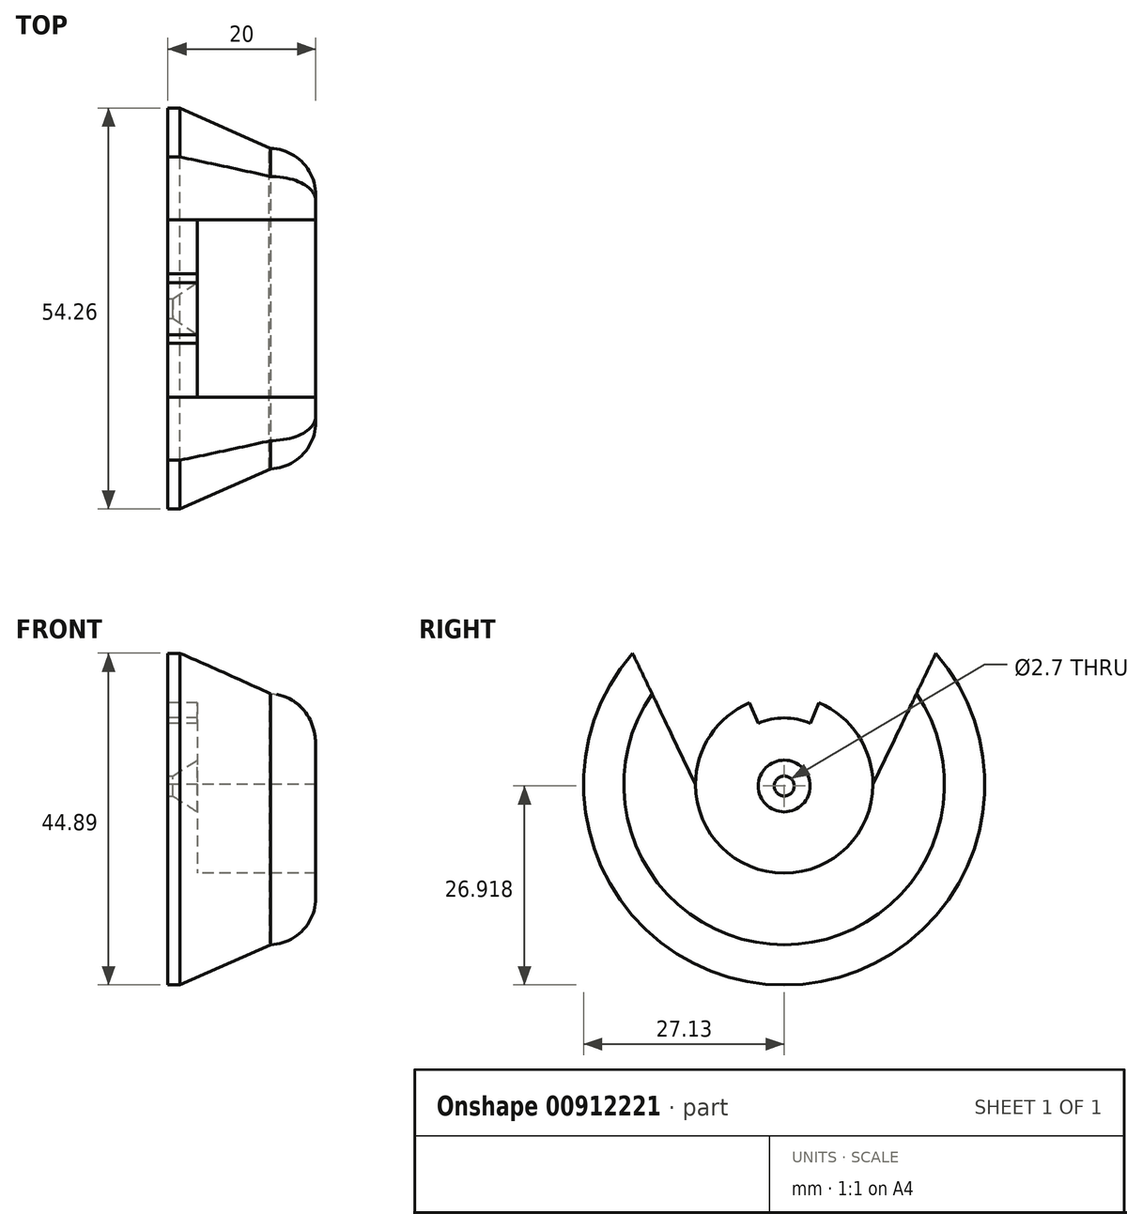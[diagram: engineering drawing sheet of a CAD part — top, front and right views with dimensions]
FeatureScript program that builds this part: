
annotation { "Feature Type Name" : "Feature", "Feature Type Description" : "" }
export const myFeature = defineFeature(function(context is Context, id is Id, definition is map)
    precondition{}
    {
        {
            var Q0;
            Q0=qCreatedBy(makeId("Right.planeOp"),FACE);
            var sketch = newSketch(context, id + "F0", { "sketchPlane" : qUnion([Q0])});
            skCircle(sketch, "E0", {"center": v(0, 0) * mm, "radius": 12 * mm});
            skCircle(sketch, "E1", {"center": v(0, 0) * mm, "radius": 30 * mm});
            skCircle(sketch, "E2", {"center": v(0, 0) * mm, "radius": 15.18 * mm});
            skCircle(sketch, "E3", {"center": v(0, 0) * mm, "radius": 27.13 * mm});
            skCircle(sketch, "E4", {"center": v(0, 0) * mm, "radius": 21.68 * mm});
            skLineSegment(sketch, "E5", {"start": v(12, 0) * mm, "end": v(21.85, 20.55) * mm});
            skLineSegment(sketch, "E6", {"start": v(21.85, 20.55) * mm, "end": v(-21.85, 20.55) * mm});
            skLineSegment(sketch, "E7", {"start": v(-21.85, 20.55) * mm, "end": v(-12, 0) * mm});
            skCircle(sketch, "E8", {"center": v(0, 0) * mm, "radius": 9 * mm});
            skLineSegment(sketch, "E9", {"start": v(0, 0) * mm, "end": v(4.69, 11.05) * mm});
            skLineSegment(sketch, "E10", {"start": v(4.69, 11.05) * mm, "end": v(-4.69, 11.05) * mm});
            skLineSegment(sketch, "E11", {"start": v(-4.69, 11.05) * mm, "end": v(0, 0) * mm});
            skSolve(sketch);
        }
        {
            var Q0;
            Q0=makeQuery(id+"F0.imprint","IMPRINT",FACE,{"disambiguationData":[TD([[makeQuery(id+"F0.imprint","IMPRINT",EDGE,{"derivedFrom":sQuery(id+"F0.wireOp",EDGE,"E0")}),-1.0]])]});
            var Q1;
            {var subQ0=sQuery(id+"F0.wireOp",EDGE,"E5");var subQ1=sQuery(id+"F0.wireOp",EDGE,"E0");var subQ2=makeQuery(id+"F0.imprint","INTERSECT",VERTEX,{"derivedFrom":[subQ1,subQ0]});Q1=makeQuery(id+"F0.imprint","IMPRINT",FACE,{"disambiguationData":[TD([[makeQuery(id+"F0.imprint","IMPRINT",EDGE,{"disambiguationData":[TD([[subQ2,1.0]])],"derivedFrom":subQ1}),-1.0]])]});}
            extrude(context, id + "F1", {"entities" : qUnion([Q0, Q1]), "depth" : 20 * mm, "offsetDistance" : 25 * mm});
        }
        {
            var Q0;
            Q0=makeQuery(id+"F0.imprint","IMPRINT",FACE,{"disambiguationData":[TD([[makeQuery(id+"F0.imprint","IMPRINT",EDGE,{"derivedFrom":sQuery(id+"F0.wireOp",EDGE,"E2")}),-1.0]])]});
            var Q1;
            {var subQ5=sQuery(id+"F0.wireOp",EDGE,"E5");var subQ6=sQuery(id+"F0.wireOp",EDGE,"E2");var subQ7=makeQuery(id+"F0.imprint","INTERSECT",VERTEX,{"derivedFrom":[subQ6,subQ5]});Q1=makeQuery(id+"F0.imprint","IMPRINT",FACE,{"disambiguationData":[TD([[makeQuery(id+"F0.imprint","IMPRINT",EDGE,{"disambiguationData":[TD([[subQ7,-1.0]])],"derivedFrom":subQ6}),-1.0]])]});}
            var Q2;
            {var subQ0=sQuery(id+"F0.wireOp",EDGE,"E6");var subQ1=sQuery(id+"F0.wireOp",EDGE,"E4");var subQ2=makeQuery(id+"F0.imprint","INTERSECT",VERTEX,{"disambiguationData":[OD(0.0)],"derivedFrom":[subQ1,subQ0]});Q2=makeQuery(id+"F0.imprint","IMPRINT",FACE,{"disambiguationData":[TD([[makeQuery(id+"F0.imprint","IMPRINT",EDGE,{"disambiguationData":[TD([[subQ2,-1.0]])],"derivedFrom":subQ1}),1.0]])]});}
            extrude(context, id + "F2", {"entities" : qUnion([Q0, Q1, Q2]), "operationType" : NewBodyOperationType.ADD, "depth" : 20 * mm, "offsetDistance" : 25 * mm});
        }
        {
            var Q0;
            Q0=makeQuery(id+"F2.opExtrude","CAP_EDGE",EDGE,{"disambiguationData":[OSD([sQuery(id+"F0.wireOp",EDGE,"E4")])],"isStart":false});
            fillet(context, id + "F3", {"entities" : qUnion([Q0]), "radius" : 6.3 * mm, "tangentPropagation" : true, "allowEdgeOverflow" : false});
        }
        {
            var Q0;
            Q0=makeQuery(id+"F0.imprint","IMPRINT",FACE,{"disambiguationData":[TD([[makeQuery(id+"F0.imprint","IMPRINT",EDGE,{"derivedFrom":sQuery(id+"F0.wireOp",EDGE,"E3")}),1.0]])]});
            extrude(context, id + "F4", {"entities" : qUnion([Q0]), "operationType" : NewBodyOperationType.ADD, "depth" : 14 * mm, "offsetDistance" : 25 * mm});
        }
        {
            var Q0;
            Q0=makeQuery(id+"F4.opExtrude","CAP_EDGE",EDGE,{"disambiguationData":[OSD([sQuery(id+"F0.wireOp",EDGE,"E3")])],"isStart":false});
            chamfer(context, id + "F5", {"entities" : qUnion([Q0]), "chamferType" : ChamferType.OFFSET_ANGLE, "width" : 5.5 * mm, "oppositeDirection" : false, "angle" : 66 * degree, "tangentPropagation" : true});
        }
        {
            var Q0;
            Q0=makeQuery(id+"F0.imprint","IMPRINT",FACE,{"disambiguationData":[TD([[makeQuery(id+"F0.imprint","IMPRINT",EDGE,{"derivedFrom":sQuery(id+"F0.wireOp",EDGE,"E0")}),1.0]])]});
            var Q1;
            {var subQ0=sQuery(id+"F0.wireOp",EDGE,"E9");var subQ1=sQuery(id+"F0.wireOp",EDGE,"E8");var subQ2=makeQuery(id+"F0.imprint","INTERSECT",VERTEX,{"derivedFrom":[subQ1,subQ0]});Q1=makeQuery(id+"F0.imprint","IMPRINT",FACE,{"disambiguationData":[TD([[makeQuery(id+"F0.imprint","IMPRINT",EDGE,{"disambiguationData":[TD([[subQ2,1.0]])],"derivedFrom":subQ1}),1.0]])]});}
            var Q2;
            {var subQ0=sQuery(id+"F0.wireOp",EDGE,"E9");var subQ1=sQuery(id+"F0.wireOp",EDGE,"E8");var subQ2=makeQuery(id+"F0.imprint","INTERSECT",VERTEX,{"derivedFrom":[subQ1,subQ0]});Q2=makeQuery(id+"F0.imprint","IMPRINT",FACE,{"disambiguationData":[TD([[makeQuery(id+"F0.imprint","IMPRINT",EDGE,{"disambiguationData":[TD([[subQ2,-1.0]])],"derivedFrom":subQ1}),1.0]])]});}
            extrude(context, id + "F6", {"entities" : qUnion([Q0, Q1, Q2]), "operationType" : NewBodyOperationType.ADD, "depth" : 4 * mm, "offsetDistance" : 25 * mm});
        }
        {
            var Q0;
            {var subQ0=sQuery(id+"F0.wireOp",EDGE,"E5");var subQ1=sQuery(id+"F0.wireOp",EDGE,"E0");var subQ2=makeQuery(id+"F0.imprint","INTERSECT",VERTEX,{"derivedFrom":[subQ1,subQ0]});Q0=makeQuery(id+"F0.imprint","IMPRINT",FACE,{"disambiguationData":[TD([[makeQuery(id+"F0.imprint","IMPRINT",EDGE,{"disambiguationData":[TD([[subQ2,-1.0]])],"derivedFrom":subQ1}),-1.0]])]});}
            var Q1;
            {var subQ5=sQuery(id+"F0.wireOp",EDGE,"E5");var subQ6=sQuery(id+"F0.wireOp",EDGE,"E2");var subQ7=makeQuery(id+"F0.imprint","INTERSECT",VERTEX,{"derivedFrom":[subQ6,subQ5]});Q1=makeQuery(id+"F0.imprint","IMPRINT",FACE,{"disambiguationData":[TD([[makeQuery(id+"F0.imprint","IMPRINT",EDGE,{"disambiguationData":[TD([[subQ7,-1.0]])],"derivedFrom":subQ6}),-1.0]])]});}
            var Q2;
            {var subQ0=sQuery(id+"F0.wireOp",EDGE,"E6");var subQ1=sQuery(id+"F0.wireOp",EDGE,"E4");var subQ2=makeQuery(id+"F0.imprint","INTERSECT",VERTEX,{"disambiguationData":[OD(0.0)],"derivedFrom":[subQ1,subQ0]});Q2=makeQuery(id+"F0.imprint","IMPRINT",FACE,{"disambiguationData":[TD([[makeQuery(id+"F0.imprint","IMPRINT",EDGE,{"disambiguationData":[TD([[subQ2,-1.0]])],"derivedFrom":subQ1}),1.0]])]});}
            var Q3;
            {var subQ0=sQuery(id+"F0.wireOp",EDGE,"E6");var subQ1=sQuery(id+"F0.wireOp",EDGE,"E3");var subQ2=makeQuery(id+"F0.imprint","INTERSECT",VERTEX,{"disambiguationData":[OD(0.0)],"derivedFrom":[subQ1,subQ0]});Q3=makeQuery(id+"F0.imprint","IMPRINT",FACE,{"disambiguationData":[TD([[makeQuery(id+"F0.imprint","IMPRINT",EDGE,{"disambiguationData":[TD([[subQ2,-1.0]])],"derivedFrom":subQ1}),1.0]])]});}
            var Q4;
            {var subQ0=sQuery(id+"F0.wireOp",EDGE,"E6");var subQ1=sQuery(id+"F0.wireOp",EDGE,"E3");var subQ2=makeQuery(id+"F0.imprint","INTERSECT",VERTEX,{"disambiguationData":[OD(1.0)],"derivedFrom":[subQ1,subQ0]});Q4=makeQuery(id+"F0.imprint","IMPRINT",FACE,{"disambiguationData":[TD([[makeQuery(id+"F0.imprint","IMPRINT",EDGE,{"disambiguationData":[TD([[subQ2,-1.0]])],"derivedFrom":subQ1}),1.0]])]});}
            var Q5;
            {var subQ0=sQuery(id+"F0.wireOp",EDGE,"E6");var subQ1=sQuery(id+"F0.wireOp",EDGE,"E3");var subQ2=makeQuery(id+"F0.imprint","INTERSECT",VERTEX,{"disambiguationData":[OD(0.0)],"derivedFrom":[subQ1,subQ0]});Q5=makeQuery(id+"F0.imprint","IMPRINT",FACE,{"disambiguationData":[TD([[makeQuery(id+"F0.imprint","IMPRINT",EDGE,{"disambiguationData":[TD([[subQ2,1.0]])],"derivedFrom":subQ1}),1.0]])]});}
            extrude(context, id + "F7", {"entities" : qUnion([Q0, Q1, Q2, Q3, Q4, Q5]), "operationType" : NewBodyOperationType.REMOVE, "depth" : 25 * mm, "offsetDistance" : 25 * mm});
        }
        {
            var Q0;
            Q0=makeQuery(id+"F6.opExtrude","CAP_FACE",FACE,{"disambiguationData":[OSD([sQuery(id+"F0.wireOp",EDGE,"E0"),sQuery(id+"F0.wireOp",EDGE,"E8"),sQuery(id+"F0.wireOp",EDGE,"E9"),sQuery(id+"F0.wireOp",EDGE,"E11")])],"isStart":false});
            var sketch = newSketch(context, id + "F8", { "sketchPlane" : qUnion([Q0])});
            skPoint(sketch, "E12", {"position": v(0, -0.21) * mm});
            skSolve(sketch);
        }
        {
            var Q0;
            Q0=sQuery(id+"F8.wireOp",VERTEX,"E12");
            var Q1;
            Q1=makeQuery(id+"F1.opExtrude","SWEPT_BODY",BODY,{"disambiguationData":[OSD([sQuery(id+"F0.wireOp",EDGE,"E0"),sQuery(id+"F0.wireOp",EDGE,"E2")])]});
            hole(context, id + "F9", {"style" : HoleStyle.C_SINK, "endStyle" : HoleEndStyle.BLIND, "holeDiameter" : 2.7 * mm, "cSinkDiameter" : 7 * mm, "cSinkAngle" : 66 * degree, "majorDiameter" : 5 * mm, "holeDepth" : 12 * mm, "isTappedThrough" : true, "tappedDepth" : 12 * mm, "tapClearance" : 3, "locations" : qUnion([Q0]), "scope" : qUnion([Q1])});
        }
    });
